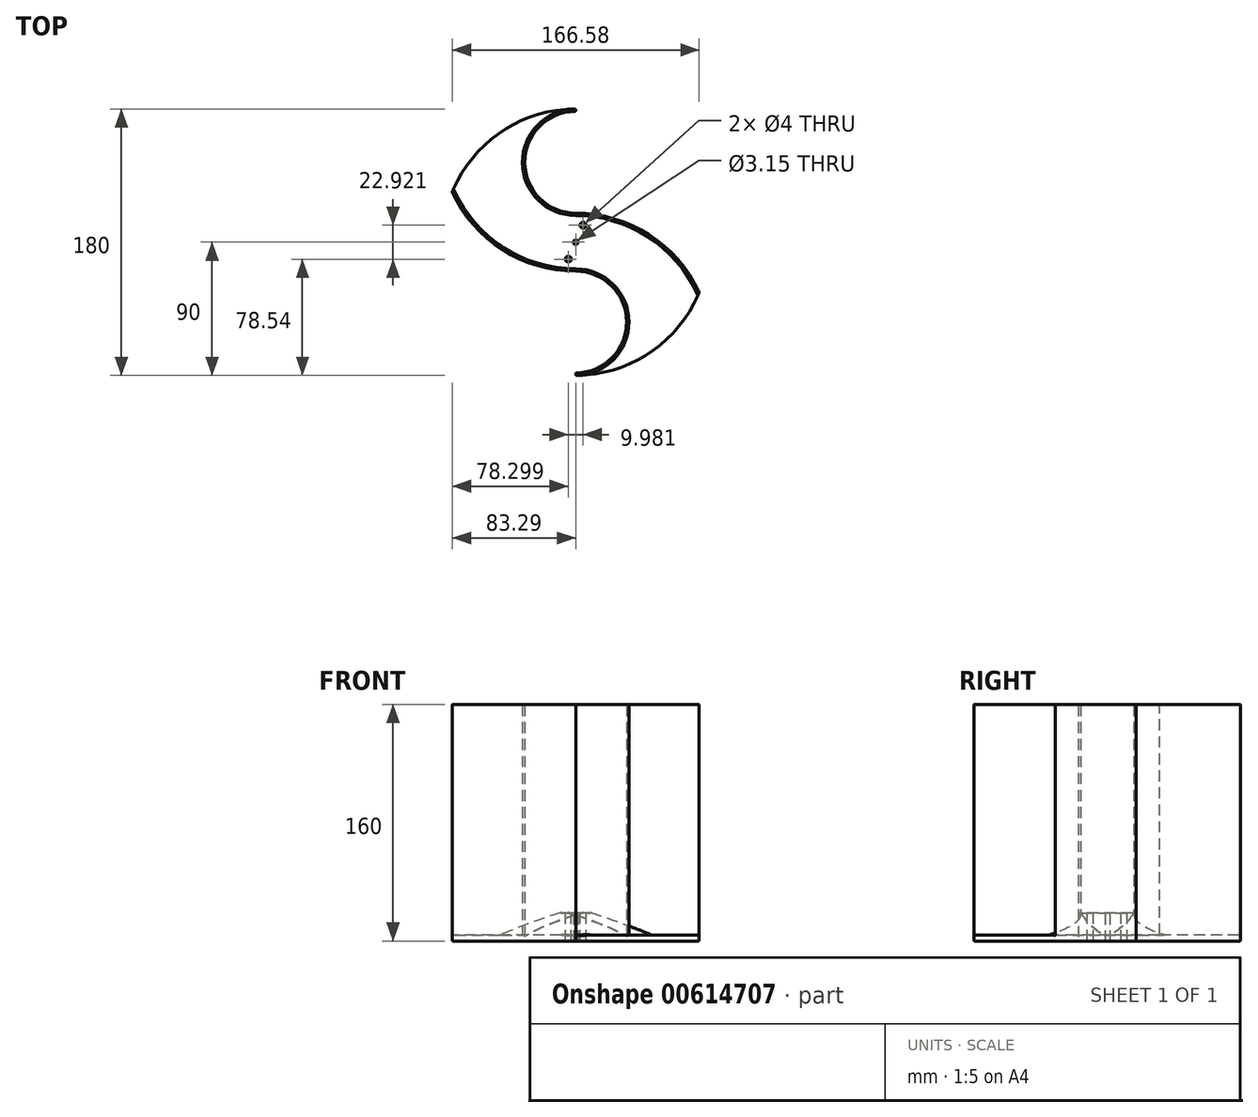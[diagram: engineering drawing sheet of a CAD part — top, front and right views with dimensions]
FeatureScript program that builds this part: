
annotation { "Feature Type Name" : "Feature", "Feature Type Description" : "" }
export const myFeature = defineFeature(function(context is Context, id is Id, definition is map)
    precondition{}
    {
        {
            var Q0;
            Q0=qCreatedBy(makeId("Top.planeOp"),FACE);
            var sketch = newSketch(context, id + "F0", { "sketchPlane" : qUnion([Q0])});
            skCircle(sketch, "E0", {"center": v(0, 0) * mm, "radius": 90 * mm});
            skArc(sketch, "E1", {"start": v(0, 90) * mm, "mid": v(-36, 54) * mm, "end": v(0, 18) * mm});
            skArc(sketch, "E2", {"start": v(0, -90) * mm, "mid": v(36, -54) * mm, "end": v(0, -18) * mm});
            skLineSegment(sketch, "E3", {"start": v(0, -90) * mm, "end": v(0, -54) * mm, "construction": true});
            skLineSegment(sketch, "E4", {"start": v(90, 0) * mm, "end": v(-90, 0) * mm, "construction": true});
            skCircle(sketch, "E5", {"center": v(0, 0) * mm, "radius": 72 * mm, "construction": true});
            skLineSegment(sketch, "E6.trimOffspring", {"start": v(0, 54) * mm, "end": v(0, 90) * mm, "construction": true});
            skArc(sketch, "E7", {"start": v(82.49, -36) * mm, "mid": v(49.3, 3.3) * mm, "end": v(0, 18) * mm});
            skArc(sketch, "E8", {"start": v(-82.49, 36) * mm, "mid": v(-49.3, -3.3) * mm, "end": v(0, -18) * mm});
            skArc(sketch, "E9.0", {"start": v(0, 88.4) * mm, "mid": v(-34.4, 54) * mm, "end": v(0, 19.6) * mm});
            skArc(sketch, "E9.1", {"start": v(83.34, -33.98) * mm, "mid": v(49.54, 5.05) * mm, "end": v(0, 19.6) * mm});
            skArc(sketch, "E10.0", {"start": v(-83.34, 33.98) * mm, "mid": v(-49.54, -5.05) * mm, "end": v(0, -19.6) * mm});
            skArc(sketch, "E10.1", {"start": v(0, -88.4) * mm, "mid": v(34.4, -54) * mm, "end": v(0, -19.6) * mm});
            skLineSegment(sketch, "E11", {"start": v(0, 88.4) * mm, "end": v(0, 90) * mm});
            skLineSegment(sketch, "E12", {"start": v(0, -88.4) * mm, "end": v(0, -90) * mm});
            skCircle(sketch, "E13", {"center": v(0, 0) * mm, "radius": 91.2 * mm});
            skCircle(sketch, "E14", {"center": v(0, 0) * mm, "radius": 20.46 * mm});
            skCircle(sketch, "E15", {"center": v(0, 0) * mm, "radius": 50.56 * mm});
            skCircle(sketch, "E16", {"center": v(0, 0) * mm, "radius": 1.57 * mm});
            skLineSegment(sketch, "E17", {"start": v(-7.9, 18.88) * mm, "end": v(-10.85, -17.34) * mm});
            skLineSegment(sketch, "E18", {"start": v(7.9, -18.88) * mm, "end": v(10.85, 17.34) * mm});
            skLineSegment(sketch, "E19", {"start": v(-32.57, 38.67) * mm, "end": v(-50.5, -2.5) * mm});
            skLineSegment(sketch, "E20", {"start": v(32.57, -38.67) * mm, "end": v(50.5, 2.5) * mm});
            skSolve(sketch);
        }
        {
            var Q0;
            {var subQ1=sQuery(id+"F0.wireOp",EDGE,"E0");var subQ3=sQuery(id+"F0.wireOp",EDGE,"E8");var subQ4=makeQuery(id+"F0.imprint","INTERSECT",VERTEX,{"derivedFrom":[subQ1,subQ3]});Q0=makeQuery(id+"F0.imprint","IMPRINT",FACE,{"disambiguationData":[TD([[makeQuery(id+"F0.imprint","IMPRINT",EDGE,{"disambiguationData":[TD([[subQ4,-1.0]])],"derivedFrom":subQ3}),1.0]])]});}
            var Q1;
            {var subQ0=sQuery(id+"F0.wireOp",EDGE,"E15");var subQ1=sQuery(id+"F0.wireOp",EDGE,"E1");var subQ2=makeQuery(id+"F0.imprint","INTERSECT",VERTEX,{"derivedFrom":[subQ1,subQ0]});Q1=makeQuery(id+"F0.imprint","IMPRINT",FACE,{"disambiguationData":[TD([[makeQuery(id+"F0.imprint","IMPRINT",EDGE,{"disambiguationData":[TD([[subQ2,-1.0]])],"derivedFrom":subQ1}),-1.0]])]});}
            var Q2;
            {var subQ0=sQuery(id+"F0.wireOp",EDGE,"E11");Q2=makeQuery(id+"F0.imprint","IMPRINT",FACE,{"disambiguationData":[TD([[makeQuery(id+"F0.imprint","IMPRINT",EDGE,{"derivedFrom":subQ0}),1.0]])]});}
            var Q3;
            {var subQ0=sQuery(id+"F0.wireOp",EDGE,"E15");var subQ1=sQuery(id+"F0.wireOp",EDGE,"E1");var subQ2=makeQuery(id+"F0.imprint","INTERSECT",VERTEX,{"derivedFrom":[subQ1,subQ0]});Q3=makeQuery(id+"F0.imprint","IMPRINT",FACE,{"disambiguationData":[TD([[makeQuery(id+"F0.imprint","IMPRINT",EDGE,{"disambiguationData":[TD([[subQ2,-1.0]])],"derivedFrom":subQ1}),1.0]])]});}
            var Q4;
            Q4=makeQuery(id+"F0.imprint","IMPRINT",FACE,{"disambiguationData":[TD([[makeQuery(id+"F0.imprint","IMPRINT",EDGE,{"derivedFrom":sQuery(id+"F0.wireOp",EDGE,"E16")}),-1.0]])]});
            var Q5;
            {var subQ0=sQuery(id+"F0.wireOp",EDGE,"E12");Q5=makeQuery(id+"F0.imprint","IMPRINT",FACE,{"disambiguationData":[TD([[makeQuery(id+"F0.imprint","IMPRINT",EDGE,{"derivedFrom":subQ0}),1.0]])]});}
            var Q6;
            {var subQ0=sQuery(id+"F0.wireOp",EDGE,"E15");var subQ1=sQuery(id+"F0.wireOp",EDGE,"E2");var subQ2=makeQuery(id+"F0.imprint","INTERSECT",VERTEX,{"derivedFrom":[subQ1,subQ0]});Q6=makeQuery(id+"F0.imprint","IMPRINT",FACE,{"disambiguationData":[TD([[makeQuery(id+"F0.imprint","IMPRINT",EDGE,{"disambiguationData":[TD([[subQ2,-1.0]])],"derivedFrom":subQ1}),-1.0]])]});}
            var Q7;
            {var subQ1=sQuery(id+"F0.wireOp",EDGE,"E0");var subQ3=sQuery(id+"F0.wireOp",EDGE,"E7");var subQ4=makeQuery(id+"F0.imprint","INTERSECT",VERTEX,{"derivedFrom":[subQ1,subQ3]});Q7=makeQuery(id+"F0.imprint","IMPRINT",FACE,{"disambiguationData":[TD([[makeQuery(id+"F0.imprint","IMPRINT",EDGE,{"disambiguationData":[TD([[subQ4,-1.0]])],"derivedFrom":subQ3}),1.0]])]});}
            var Q8;
            {var subQ0=sQuery(id+"F0.wireOp",EDGE,"E7");var subQ1=sQuery(id+"F0.wireOp",EDGE,"E0");var subQ2=makeQuery(id+"F0.imprint","INTERSECT",VERTEX,{"derivedFrom":[subQ1,subQ0]});Q8=makeQuery(id+"F0.imprint","IMPRINT",FACE,{"disambiguationData":[TD([[makeQuery(id+"F0.imprint","IMPRINT",EDGE,{"disambiguationData":[TD([[subQ2,-1.0]])],"derivedFrom":subQ1}),1.0]])]});}
            var Q9;
            {var subQ0=sQuery(id+"F0.wireOp",EDGE,"E15");var subQ1=sQuery(id+"F0.wireOp",EDGE,"E7");var subQ2=makeQuery(id+"F0.imprint","INTERSECT",VERTEX,{"derivedFrom":[subQ1,subQ0]});Q9=makeQuery(id+"F0.imprint","IMPRINT",FACE,{"disambiguationData":[TD([[makeQuery(id+"F0.imprint","IMPRINT",EDGE,{"disambiguationData":[TD([[subQ2,-1.0]])],"derivedFrom":subQ1}),-1.0]])]});}
            var Q10;
            {var subQ5=sQuery(id+"F0.wireOp",EDGE,"E7");var subQ6=sQuery(id+"F0.wireOp",EDGE,"E1");var subQ7=makeQuery(id+"F0.imprint","INTERSECT",VERTEX,{"derivedFrom":[subQ6,subQ5]});Q10=makeQuery(id+"F0.imprint","IMPRINT",FACE,{"disambiguationData":[TD([[makeQuery(id+"F0.imprint","IMPRINT",EDGE,{"disambiguationData":[TD([[subQ7,1.0]])],"derivedFrom":subQ6}),1.0]])]});}
            var Q11;
            {var subQ5=sQuery(id+"F0.wireOp",EDGE,"E8");var subQ6=sQuery(id+"F0.wireOp",EDGE,"E2");var subQ7=makeQuery(id+"F0.imprint","INTERSECT",VERTEX,{"derivedFrom":[subQ6,subQ5]});Q11=makeQuery(id+"F0.imprint","IMPRINT",FACE,{"disambiguationData":[TD([[makeQuery(id+"F0.imprint","IMPRINT",EDGE,{"disambiguationData":[TD([[subQ7,1.0]])],"derivedFrom":subQ6}),1.0]])]});}
            var Q12;
            {var subQ0=sQuery(id+"F0.wireOp",EDGE,"E15");var subQ1=sQuery(id+"F0.wireOp",EDGE,"E2");var subQ2=makeQuery(id+"F0.imprint","INTERSECT",VERTEX,{"derivedFrom":[subQ1,subQ0]});Q12=makeQuery(id+"F0.imprint","IMPRINT",FACE,{"disambiguationData":[TD([[makeQuery(id+"F0.imprint","IMPRINT",EDGE,{"disambiguationData":[TD([[subQ2,-1.0]])],"derivedFrom":subQ1}),1.0]])]});}
            var Q13;
            {var subQ0=sQuery(id+"F0.wireOp",EDGE,"E15");var subQ1=sQuery(id+"F0.wireOp",EDGE,"E8");var subQ2=makeQuery(id+"F0.imprint","INTERSECT",VERTEX,{"derivedFrom":[subQ1,subQ0]});Q13=makeQuery(id+"F0.imprint","IMPRINT",FACE,{"disambiguationData":[TD([[makeQuery(id+"F0.imprint","IMPRINT",EDGE,{"disambiguationData":[TD([[subQ2,-1.0]])],"derivedFrom":subQ1}),-1.0]])]});}
            var Q14;
            {var subQ0=sQuery(id+"F0.wireOp",EDGE,"E8");var subQ1=sQuery(id+"F0.wireOp",EDGE,"E0");var subQ2=makeQuery(id+"F0.imprint","INTERSECT",VERTEX,{"derivedFrom":[subQ1,subQ0]});Q14=makeQuery(id+"F0.imprint","IMPRINT",FACE,{"disambiguationData":[TD([[makeQuery(id+"F0.imprint","IMPRINT",EDGE,{"disambiguationData":[TD([[subQ2,-1.0]])],"derivedFrom":subQ1}),1.0]])]});}
            var Q15;
            {var subQ0=sQuery(id+"F0.wireOp",EDGE,"E19");Q15=makeQuery(id+"F0.imprint","IMPRINT",FACE,{"disambiguationData":[TD([[makeQuery(id+"F0.imprint","IMPRINT",EDGE,{"derivedFrom":subQ0}),-1.0]])]});}
            var Q16;
            {var subQ0=sQuery(id+"F0.wireOp",EDGE,"E17");Q16=makeQuery(id+"F0.imprint","IMPRINT",FACE,{"disambiguationData":[TD([[makeQuery(id+"F0.imprint","IMPRINT",EDGE,{"derivedFrom":subQ0}),-1.0]])]});}
            var Q17;
            {var subQ0=sQuery(id+"F0.wireOp",EDGE,"E18");Q17=makeQuery(id+"F0.imprint","IMPRINT",FACE,{"disambiguationData":[TD([[makeQuery(id+"F0.imprint","IMPRINT",EDGE,{"derivedFrom":subQ0}),-1.0]])]});}
            var Q18;
            {var subQ0=sQuery(id+"F0.wireOp",EDGE,"E20");Q18=makeQuery(id+"F0.imprint","IMPRINT",FACE,{"disambiguationData":[TD([[makeQuery(id+"F0.imprint","IMPRINT",EDGE,{"derivedFrom":subQ0}),-1.0]])]});}
            extrude(context, id + "F1", {"entities" : qUnion([Q0, Q1, Q2, Q3, Q4, Q5, Q6, Q7, Q8, Q9, Q10, Q11, Q12, Q13, Q14, Q15, Q16, Q17, Q18]), "depth" : 4 * mm, "offsetDistance" : 25 * mm});
        }
        {
            var Q0;
            Q0=makeQuery(id+"F0.imprint","IMPRINT",FACE,{"disambiguationData":[TD([[makeQuery(id+"F0.imprint","IMPRINT",EDGE,{"derivedFrom":sQuery(id+"F0.wireOp",EDGE,"E2")}),1.0]])]});
            var Q1;
            Q1=makeQuery(id+"F0.imprint","IMPRINT",FACE,{"disambiguationData":[TD([[makeQuery(id+"F0.imprint","IMPRINT",EDGE,{"derivedFrom":sQuery(id+"F0.wireOp",EDGE,"E1")}),1.0]])]});
            var Q2;
            {var subQ5=sQuery(id+"F0.wireOp",EDGE,"E8");var subQ6=sQuery(id+"F0.wireOp",EDGE,"E2");var subQ7=makeQuery(id+"F0.imprint","INTERSECT",VERTEX,{"derivedFrom":[subQ6,subQ5]});Q2=makeQuery(id+"F0.imprint","IMPRINT",FACE,{"disambiguationData":[TD([[makeQuery(id+"F0.imprint","IMPRINT",EDGE,{"disambiguationData":[TD([[subQ7,1.0]])],"derivedFrom":subQ6}),1.0]])]});}
            var Q3;
            {var subQ0=sQuery(id+"F0.wireOp",EDGE,"E15");var subQ1=sQuery(id+"F0.wireOp",EDGE,"E8");var subQ2=makeQuery(id+"F0.imprint","INTERSECT",VERTEX,{"derivedFrom":[subQ1,subQ0]});Q3=makeQuery(id+"F0.imprint","IMPRINT",FACE,{"disambiguationData":[TD([[makeQuery(id+"F0.imprint","IMPRINT",EDGE,{"disambiguationData":[TD([[subQ2,-1.0]])],"derivedFrom":subQ1}),-1.0]])]});}
            var Q4;
            {var subQ0=sQuery(id+"F0.wireOp",EDGE,"E8");var subQ1=sQuery(id+"F0.wireOp",EDGE,"E0");var subQ2=makeQuery(id+"F0.imprint","INTERSECT",VERTEX,{"derivedFrom":[subQ1,subQ0]});Q4=makeQuery(id+"F0.imprint","IMPRINT",FACE,{"disambiguationData":[TD([[makeQuery(id+"F0.imprint","IMPRINT",EDGE,{"disambiguationData":[TD([[subQ2,-1.0]])],"derivedFrom":subQ1}),1.0]])]});}
            var Q5;
            {var subQ5=sQuery(id+"F0.wireOp",EDGE,"E7");var subQ6=sQuery(id+"F0.wireOp",EDGE,"E1");var subQ7=makeQuery(id+"F0.imprint","INTERSECT",VERTEX,{"derivedFrom":[subQ6,subQ5]});Q5=makeQuery(id+"F0.imprint","IMPRINT",FACE,{"disambiguationData":[TD([[makeQuery(id+"F0.imprint","IMPRINT",EDGE,{"disambiguationData":[TD([[subQ7,1.0]])],"derivedFrom":subQ6}),1.0]])]});}
            var Q6;
            {var subQ0=sQuery(id+"F0.wireOp",EDGE,"E15");var subQ1=sQuery(id+"F0.wireOp",EDGE,"E7");var subQ2=makeQuery(id+"F0.imprint","INTERSECT",VERTEX,{"derivedFrom":[subQ1,subQ0]});Q6=makeQuery(id+"F0.imprint","IMPRINT",FACE,{"disambiguationData":[TD([[makeQuery(id+"F0.imprint","IMPRINT",EDGE,{"disambiguationData":[TD([[subQ2,-1.0]])],"derivedFrom":subQ1}),-1.0]])]});}
            var Q7;
            {var subQ0=sQuery(id+"F0.wireOp",EDGE,"E7");var subQ1=sQuery(id+"F0.wireOp",EDGE,"E0");var subQ2=makeQuery(id+"F0.imprint","INTERSECT",VERTEX,{"derivedFrom":[subQ1,subQ0]});Q7=makeQuery(id+"F0.imprint","IMPRINT",FACE,{"disambiguationData":[TD([[makeQuery(id+"F0.imprint","IMPRINT",EDGE,{"disambiguationData":[TD([[subQ2,-1.0]])],"derivedFrom":subQ1}),1.0]])]});}
            extrude(context, id + "F2", {"entities" : qUnion([Q0, Q1, Q2, Q3, Q4, Q5, Q6, Q7]), "operationType" : NewBodyOperationType.ADD, "depth" : 160 * mm, "offsetDistance" : 25 * mm});
        }
        {
            var Q0;
            Q0=makeQuery(id+"F2.opExtrude","SWEPT_EDGE",EDGE,{"disambiguationData":[OSD([sQuery(id+"F0.wireOp",EDGE,"E0"),sQuery(id+"F0.wireOp",EDGE,"E8")])]});
            var Q1;
            Q1=makeQuery(id+"F2.opExtrude","SWEPT_EDGE",EDGE,{"disambiguationData":[OSD([sQuery(id+"F0.wireOp",EDGE,"E0"),sQuery(id+"F0.wireOp",EDGE,"E10.0")])]});
            var Q2;
            Q2=makeQuery(id+"F2.opExtrude","SWEPT_EDGE",EDGE,{"disambiguationData":[OSD([sQuery(id+"F0.wireOp",EDGE,"E0"),sQuery(id+"F0.wireOp",EDGE,"E1"),sQuery(id+"F0.wireOp",EDGE,"E11")])]});
            var Q3;
            Q3=makeQuery(id+"F2.opExtrude","SWEPT_EDGE",EDGE,{"disambiguationData":[OSD([sQuery(id+"F0.wireOp",EDGE,"E9.0"),sQuery(id+"F0.wireOp",EDGE,"E11")])]});
            var Q4;
            Q4=makeQuery(id+"F2.opExtrude","SWEPT_EDGE",EDGE,{"disambiguationData":[OSD([sQuery(id+"F0.wireOp",EDGE,"E0"),sQuery(id+"F0.wireOp",EDGE,"E7")])]});
            var Q5;
            Q5=makeQuery(id+"F2.opExtrude","SWEPT_EDGE",EDGE,{"disambiguationData":[OSD([sQuery(id+"F0.wireOp",EDGE,"E0"),sQuery(id+"F0.wireOp",EDGE,"E9.1")])]});
            var Q6;
            Q6=makeQuery(id+"F2.opExtrude","SWEPT_EDGE",EDGE,{"disambiguationData":[OSD([sQuery(id+"F0.wireOp",EDGE,"E10.1"),sQuery(id+"F0.wireOp",EDGE,"E12")])]});
            var Q7;
            Q7=makeQuery(id+"F2.opExtrude","SWEPT_EDGE",EDGE,{"disambiguationData":[OSD([sQuery(id+"F0.wireOp",EDGE,"E0"),sQuery(id+"F0.wireOp",EDGE,"E2"),sQuery(id+"F0.wireOp",EDGE,"E12")])]});
            fillet(context, id + "F3", {"entities" : qUnion([Q0, Q1, Q2, Q3, Q4, Q5, Q6, Q7]), "radius" : 0.5 * mm, "tangentPropagation" : true, "allowEdgeOverflow" : false});
        }
        {
            var Q0;
            Q0=makeQuery(id+"F0.imprint","IMPRINT",FACE,{"disambiguationData":[TD([[makeQuery(id+"F0.imprint","IMPRINT",EDGE,{"derivedFrom":sQuery(id+"F0.wireOp",EDGE,"E16")}),-1.0]])]});
            var Q1;
            {var subQ0=sQuery(id+"F0.wireOp",EDGE,"E15");var subQ1=sQuery(id+"F0.wireOp",EDGE,"E1");var subQ2=makeQuery(id+"F0.imprint","INTERSECT",VERTEX,{"derivedFrom":[subQ1,subQ0]});Q1=makeQuery(id+"F0.imprint","IMPRINT",FACE,{"disambiguationData":[TD([[makeQuery(id+"F0.imprint","IMPRINT",EDGE,{"disambiguationData":[TD([[subQ2,-1.0]])],"derivedFrom":subQ1}),-1.0]])]});}
            var Q2;
            {var subQ0=sQuery(id+"F0.wireOp",EDGE,"E15");var subQ1=sQuery(id+"F0.wireOp",EDGE,"E2");var subQ2=makeQuery(id+"F0.imprint","INTERSECT",VERTEX,{"derivedFrom":[subQ1,subQ0]});Q2=makeQuery(id+"F0.imprint","IMPRINT",FACE,{"disambiguationData":[TD([[makeQuery(id+"F0.imprint","IMPRINT",EDGE,{"disambiguationData":[TD([[subQ2,-1.0]])],"derivedFrom":subQ1}),-1.0]])]});}
            var Q3;
            {var subQ0=sQuery(id+"F0.wireOp",EDGE,"E17");Q3=makeQuery(id+"F0.imprint","IMPRINT",FACE,{"disambiguationData":[TD([[makeQuery(id+"F0.imprint","IMPRINT",EDGE,{"derivedFrom":subQ0}),-1.0]])]});}
            var Q4;
            {var subQ0=sQuery(id+"F0.wireOp",EDGE,"E18");Q4=makeQuery(id+"F0.imprint","IMPRINT",FACE,{"disambiguationData":[TD([[makeQuery(id+"F0.imprint","IMPRINT",EDGE,{"derivedFrom":subQ0}),-1.0]])]});}
            extrude(context, id + "F4", {"entities" : qUnion([Q0, Q1, Q2, Q3, Q4]), "operationType" : NewBodyOperationType.ADD, "depth" : 19 * mm, "offsetDistance" : 25 * mm});
        }
        {
            var Q0;
            Q0=makeQuery(id+"F4.opExtrude","CAP_EDGE",EDGE,{"disambiguationData":[OSD([sQuery(id+"F0.wireOp",EDGE,"E19")])],"isStart":false});
            var Q1;
            Q1=makeQuery(id+"F4.opExtrude","CAP_EDGE",EDGE,{"disambiguationData":[OSD([sQuery(id+"F0.wireOp",EDGE,"E20")])],"isStart":false});
            chamfer(context, id + "F5", {"entities" : qUnion([Q0, Q1]), "chamferType" : ChamferType.TWO_OFFSETS, "width1" : 43 * mm, "oppositeDirection" : false, "width2" : 15 * mm, "tangentPropagation" : true});
        }
        {
            var Q0;
            Q0=makeQuery(id+"F5.opChamfer","BLEND_FACE",FACE,{"disambiguationData":[OSD([sQuery(id+"F0.wireOp",EDGE,"E20")])]});
            var Q1;
            Q1=makeQuery(id+"F5.opChamfer","BLEND_FACE",FACE,{"disambiguationData":[OSD([sQuery(id+"F0.wireOp",EDGE,"E19")])]});
            var Q2;
            Q2=makeQuery(id+"F4.opExtrude","CAP_FACE",FACE,{"disambiguationData":[OSD([sQuery(id+"F0.wireOp",EDGE,"E1"),sQuery(id+"F0.wireOp",EDGE,"E2"),sQuery(id+"F0.wireOp",EDGE,"E7"),sQuery(id+"F0.wireOp",EDGE,"E8"),sQuery(id+"F0.wireOp",EDGE,"E16"),sQuery(id+"F0.wireOp",EDGE,"E19"),sQuery(id+"F0.wireOp",EDGE,"E20")])],"isStart":false});
            fillet(context, id + "F6", {"entities" : qUnion([Q0, Q1, Q2]), "radius" : 0.4 * mm, "tangentPropagation" : true, "allowEdgeOverflow" : false});
        }
        {
            var Q0;
            {var subQ0=sQuery(id+"F0.wireOp",EDGE,"E0");var subQ1=makeQuery(id+"F0.imprint","INTERSECT",VERTEX,{"derivedFrom":[subQ0,sQuery(id+"F0.wireOp",EDGE,"E7")]});var subQ2=makeQuery(id+"F0.imprint","IMPRINT",EDGE,{"disambiguationData":[TD([[subQ1,-1.0]])],"derivedFrom":subQ0});Q0=makeQuery(id+"F2.boolean.opBoolean","MERGE",FACE,{"derivedFrom":[makeQuery(id+"F1.opExtrude","SWEPT_FACE",FACE,{"disambiguationData":[OSD([subQ0]),TDD([makeQuery(id+"F0.imprint","IMPRINT",EDGE,{"disambiguationData":[TD([[subQ1,1.0]])],"derivedFrom":subQ0}),subQ2])]}),makeQuery(id+"F2.opExtrude","SWEPT_FACE",FACE,{"disambiguationData":[OSD([subQ0]),TDD([subQ2])]})]});}
            var Q1;
            {var subQ0=sQuery(id+"F0.wireOp",EDGE,"E0");var subQ1=makeQuery(id+"F0.imprint","INTERSECT",VERTEX,{"derivedFrom":[subQ0,sQuery(id+"F0.wireOp",EDGE,"E8")]});var subQ2=makeQuery(id+"F0.imprint","IMPRINT",EDGE,{"disambiguationData":[TD([[subQ1,-1.0]])],"derivedFrom":subQ0});Q1=makeQuery(id+"F2.boolean.opBoolean","MERGE",FACE,{"derivedFrom":[makeQuery(id+"F1.opExtrude","SWEPT_FACE",FACE,{"disambiguationData":[OSD([subQ0]),TDD([makeQuery(id+"F0.imprint","IMPRINT",EDGE,{"disambiguationData":[TD([[subQ1,1.0]])],"derivedFrom":subQ0}),subQ2])]}),makeQuery(id+"F2.opExtrude","SWEPT_FACE",FACE,{"disambiguationData":[OSD([subQ0]),TDD([subQ2])]})]});}
            var Q2;
            Q2=makeQuery(id+"F2.boolean.opBoolean","INTERSECT",EDGE,{"derivedFrom":[makeQuery(id+"F1.opExtrude","CAP_FACE",FACE,{"disambiguationData":[OSD([sQuery(id+"F0.wireOp",EDGE,"E0"),sQuery(id+"F0.wireOp",EDGE,"E9.0"),sQuery(id+"F0.wireOp",EDGE,"E9.1"),sQuery(id+"F0.wireOp",EDGE,"E10.0"),sQuery(id+"F0.wireOp",EDGE,"E10.1"),sQuery(id+"F0.wireOp",EDGE,"E11"),sQuery(id+"F0.wireOp",EDGE,"E12"),sQuery(id+"F0.wireOp",EDGE,"E16")])],"isStart":false}),makeQuery(id+"F2.opExtrude","SWEPT_FACE",FACE,{"disambiguationData":[OSD([sQuery(id+"F0.wireOp",EDGE,"E8")])]})]});
            var Q3;
            {var subQ0=sQuery(id+"F0.wireOp",EDGE,"E0");var subQ1=makeQuery(id+"F0.imprint","INTERSECT",VERTEX,{"derivedFrom":[subQ0,sQuery(id+"F0.wireOp",EDGE,"E7")]});Q3=makeQuery(id+"F1.opExtrude","CAP_EDGE",EDGE,{"disambiguationData":[OSD([subQ0]),TDD([makeQuery(id+"F0.imprint","IMPRINT",EDGE,{"disambiguationData":[TD([[subQ1,1.0]])],"derivedFrom":subQ0}),makeQuery(id+"F0.imprint","IMPRINT",EDGE,{"disambiguationData":[TD([[subQ1,-1.0]])],"derivedFrom":subQ0})])],"isStart":false});}
            var Q4;
            Q4=makeQuery(id+"F2.boolean.opBoolean","INTERSECT",EDGE,{"derivedFrom":[makeQuery(id+"F1.opExtrude","CAP_FACE",FACE,{"disambiguationData":[OSD([sQuery(id+"F0.wireOp",EDGE,"E0"),sQuery(id+"F0.wireOp",EDGE,"E9.0"),sQuery(id+"F0.wireOp",EDGE,"E9.1"),sQuery(id+"F0.wireOp",EDGE,"E10.0"),sQuery(id+"F0.wireOp",EDGE,"E10.1"),sQuery(id+"F0.wireOp",EDGE,"E11"),sQuery(id+"F0.wireOp",EDGE,"E12"),sQuery(id+"F0.wireOp",EDGE,"E16")])],"isStart":false}),makeQuery(id+"F2.opExtrude","SWEPT_FACE",FACE,{"disambiguationData":[OSD([sQuery(id+"F0.wireOp",EDGE,"E7")])]})]});
            fillet(context, id + "F7", {"entities" : qUnion([Q0, Q1, Q2, Q3, Q4]), "radius" : 0.4 * mm, "tangentPropagation" : true, "allowEdgeOverflow" : false});
        }
        {
            var Q0;
            Q0=makeQuery(id+"F2.boolean.opBoolean","INTERSECT",EDGE,{"derivedFrom":[makeQuery(id+"F1.opExtrude","CAP_FACE",FACE,{"disambiguationData":[OSD([sQuery(id+"F0.wireOp",EDGE,"E0"),sQuery(id+"F0.wireOp",EDGE,"E9.0"),sQuery(id+"F0.wireOp",EDGE,"E9.1"),sQuery(id+"F0.wireOp",EDGE,"E10.0"),sQuery(id+"F0.wireOp",EDGE,"E10.1"),sQuery(id+"F0.wireOp",EDGE,"E11"),sQuery(id+"F0.wireOp",EDGE,"E12"),sQuery(id+"F0.wireOp",EDGE,"E16")])],"isStart":false}),makeQuery(id+"F2.opExtrude","SWEPT_FACE",FACE,{"disambiguationData":[OSD([sQuery(id+"F0.wireOp",EDGE,"E2")])]})]});
            var Q1;
            Q1=makeQuery(id+"F2.boolean.opBoolean","INTERSECT",EDGE,{"derivedFrom":[makeQuery(id+"F1.opExtrude","CAP_FACE",FACE,{"disambiguationData":[OSD([sQuery(id+"F0.wireOp",EDGE,"E0"),sQuery(id+"F0.wireOp",EDGE,"E9.0"),sQuery(id+"F0.wireOp",EDGE,"E9.1"),sQuery(id+"F0.wireOp",EDGE,"E10.0"),sQuery(id+"F0.wireOp",EDGE,"E10.1"),sQuery(id+"F0.wireOp",EDGE,"E11"),sQuery(id+"F0.wireOp",EDGE,"E12"),sQuery(id+"F0.wireOp",EDGE,"E16")])],"isStart":false}),makeQuery(id+"F2.opExtrude","SWEPT_FACE",FACE,{"disambiguationData":[OSD([sQuery(id+"F0.wireOp",EDGE,"E1")])]})]});
            fillet(context, id + "F8", {"entities" : qUnion([Q0, Q1]), "radius" : 0.4 * mm, "tangentPropagation" : true, "allowEdgeOverflow" : false});
        }
        {
            var Q0;
            Q0=makeQuery(id+"F4.opExtrude","CAP_FACE",FACE,{"disambiguationData":[OSD([sQuery(id+"F0.wireOp",EDGE,"E1"),sQuery(id+"F0.wireOp",EDGE,"E2"),sQuery(id+"F0.wireOp",EDGE,"E7"),sQuery(id+"F0.wireOp",EDGE,"E8"),sQuery(id+"F0.wireOp",EDGE,"E16"),sQuery(id+"F0.wireOp",EDGE,"E19"),sQuery(id+"F0.wireOp",EDGE,"E20")])],"isStart":false});
            var sketch = newSketch(context, id + "F9", { "sketchPlane" : qUnion([Q0])});
            skCircle(sketch, "E21", {"center": v(5, 11.46) * mm, "radius": 2 * mm});
            skCircle(sketch, "E22", {"center": v(-5, -11.46) * mm, "radius": 2 * mm});
            skSolve(sketch);
        }
        {
            var Q0;
            Q0=makeQuery(id+"F9.imprint","IMPRINT",FACE,{"disambiguationData":[TD([[makeQuery(id+"F9.imprint","IMPRINT",EDGE,{"derivedFrom":sQuery(id+"F9.wireOp",EDGE,"E21")}),1.0]])]});
            var Q1;
            Q1=makeQuery(id+"F9.imprint","IMPRINT",FACE,{"disambiguationData":[TD([[makeQuery(id+"F9.imprint","IMPRINT",EDGE,{"derivedFrom":sQuery(id+"F9.wireOp",EDGE,"E22")}),1.0]])]});
            extrude(context, id + "F10", {"entities" : qUnion([Q0, Q1]), "operationType" : NewBodyOperationType.REMOVE, "oppositeDirection" : true, "depth" : 25 * mm, "offsetDistance" : 25 * mm});
        }
    });
